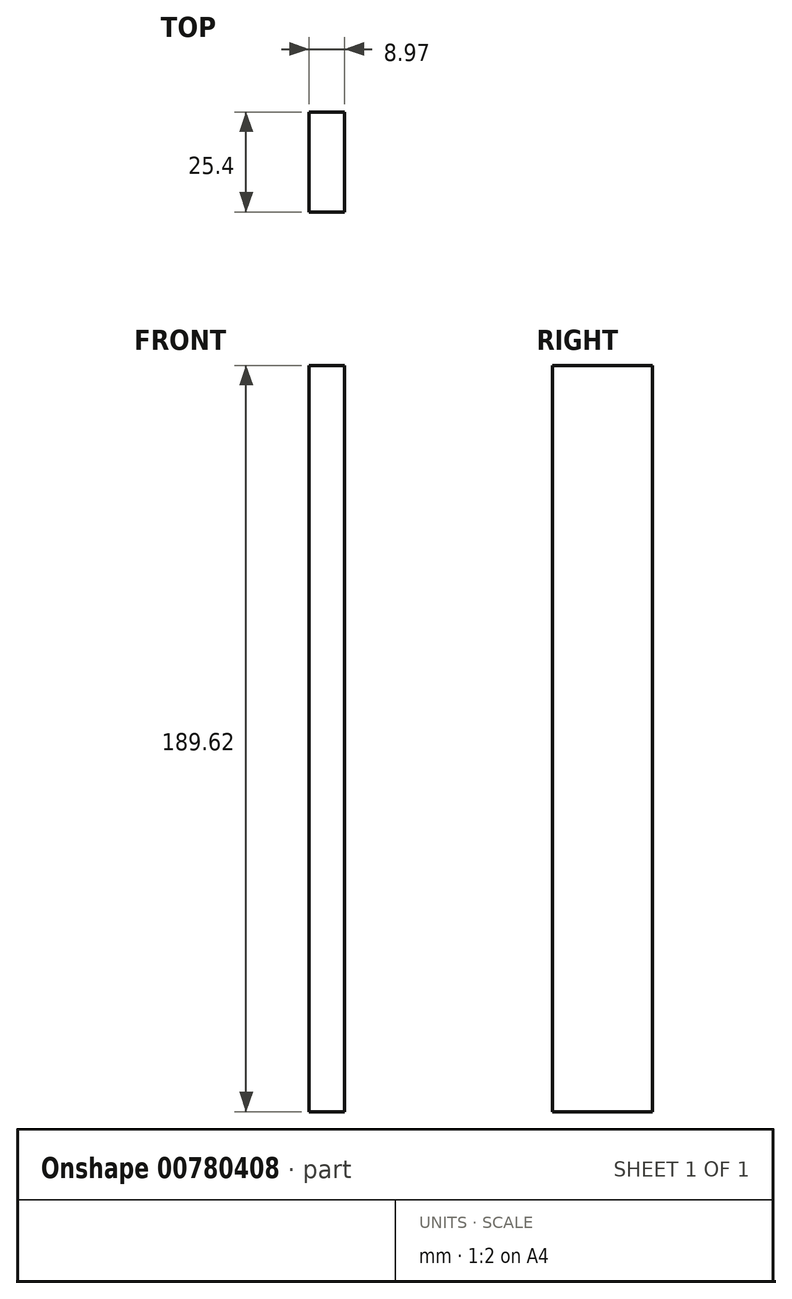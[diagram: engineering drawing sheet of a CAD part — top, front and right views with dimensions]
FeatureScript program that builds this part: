
annotation { "Feature Type Name" : "Feature", "Feature Type Description" : "" }
export const myFeature = defineFeature(function(context is Context, id is Id, definition is map)
    precondition{}
    {
        {
            var Q0;
            Q0=qCreatedBy(makeId("Front.planeOp"),FACE);
            var sketch = newSketch(context, id + "F0", { "sketchPlane" : qUnion([Q0])});
            skLineSegment(sketch, "E0.bottom", {"start": v(0, 0) * mm, "end": v(0, 0) * mm});
            skLineSegment(sketch, "E0.top", {"start": v(0, 0) * mm, "end": v(0, 0) * mm});
            skLineSegment(sketch, "E0.left", {"start": v(0, 0) * mm, "end": v(0, 0) * mm});
            skLineSegment(sketch, "E0.right", {"start": v(0, 0) * mm, "end": v(0, 0) * mm});
            skPoint(sketch, "E0.middle", {"position": v(0, 0) * mm});
            skLineSegment(sketch, "E1.bottom", {"start": v(39.67, 0) * mm, "end": v(43.54, 0) * mm});
            skLineSegment(sketch, "E1.top", {"start": v(39.67, 0) * mm, "end": v(43.54, 0) * mm});
            skLineSegment(sketch, "E1.left", {"start": v(39.67, 0) * mm, "end": v(39.67, 0) * mm});
            skLineSegment(sketch, "E1.right", {"start": v(43.54, 0) * mm, "end": v(43.54, 0) * mm});
            skLineSegment(sketch, "E2.bottom", {"start": v(8.97, 278.58) * mm, "end": v(0, 278.58) * mm});
            skLineSegment(sketch, "E2.top", {"start": v(8.97, 88.96) * mm, "end": v(0, 88.96) * mm});
            skLineSegment(sketch, "E2.left", {"start": v(8.97, 278.58) * mm, "end": v(8.97, 88.96) * mm});
            skLineSegment(sketch, "E2.right", {"start": v(0, 278.58) * mm, "end": v(0, 88.96) * mm});
            skSolve(sketch);
        }
        {
            var Q0;
            Q0=sQuery(id+"F0.wireOp",EDGE,"E2.right");
            var Q1;
            Q1=sQuery(id+"F0.wireOp",EDGE,"E2.top");
            var Q2;
            Q2=sQuery(id+"F0.wireOp",EDGE,"E2.left");
            var Q3;
            Q3=sQuery(id+"F0.wireOp",EDGE,"E2.bottom");
            extrude(context, id + "F1", {"bodyType" : ToolBodyType.SURFACE, "surfaceEntities" : qUnion([Q0, Q1, Q2, Q3]), "depth" : 25.4 * mm, "offsetDistance" : 25.4 * mm});
        }
    });
